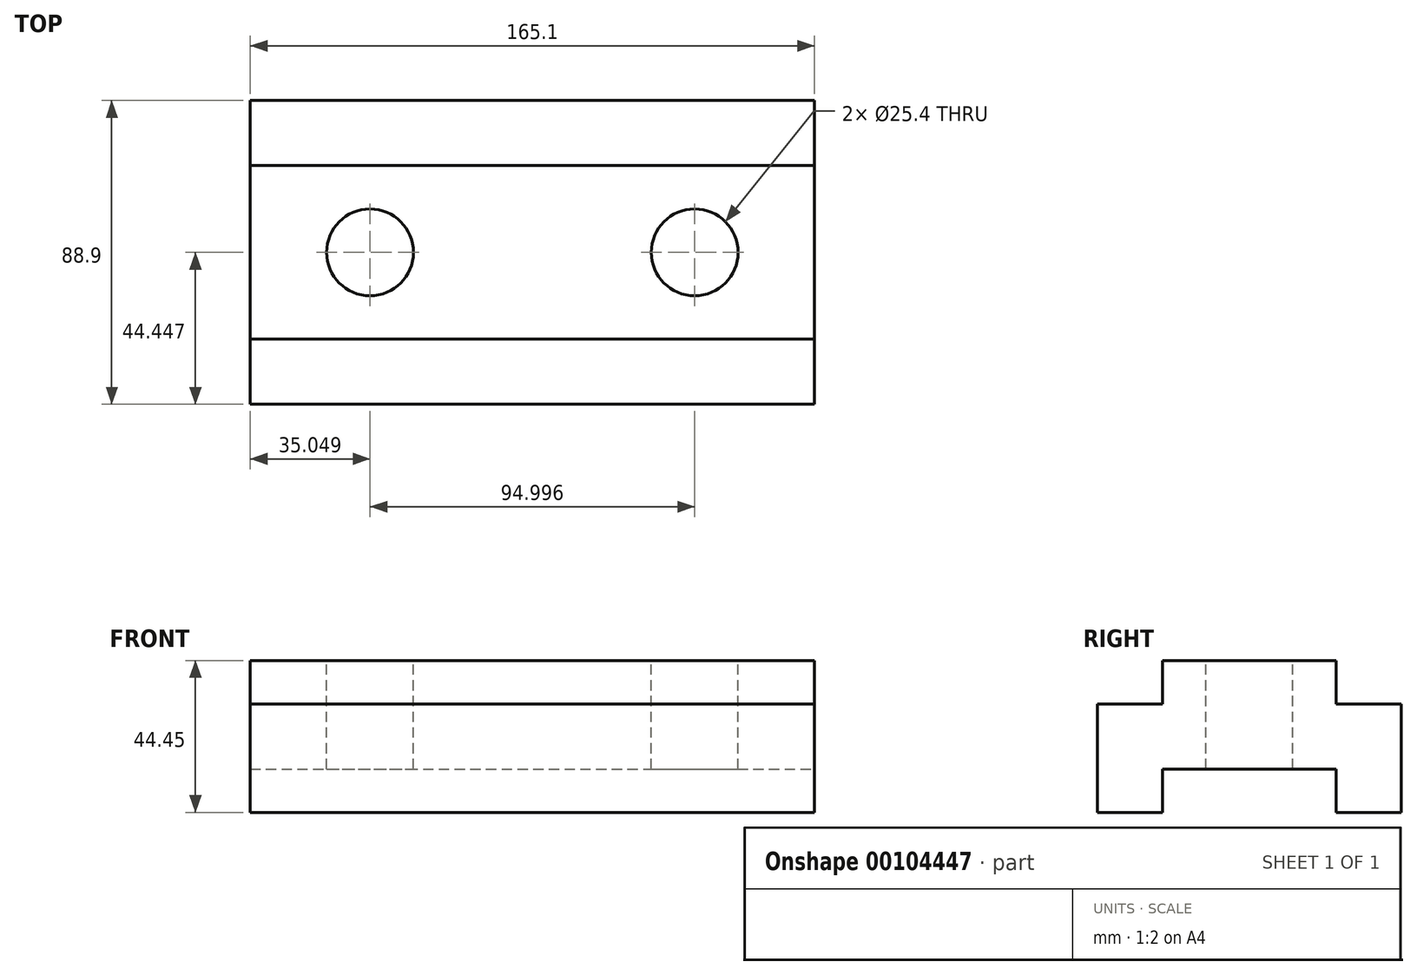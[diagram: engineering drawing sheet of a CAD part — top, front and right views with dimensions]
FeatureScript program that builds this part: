
annotation { "Feature Type Name" : "Feature", "Feature Type Description" : "" }
export const myFeature = defineFeature(function(context is Context, id is Id, definition is map)
    precondition{}
    {
        {
            var Q0;
            Q0=qCreatedBy(makeId("Top.planeOp"),FACE);
            var sketch = newSketch(context, id + "F0", { "sketchPlane" : qUnion([Q0])});
            skLineSegment(sketch, "E0.bottom", {"start": v(-108.37, 36.42) * mm, "end": v(56.73, 36.42) * mm});
            skLineSegment(sketch, "E0.top", {"start": v(-108.37, -52.48) * mm, "end": v(56.73, -52.48) * mm});
            skLineSegment(sketch, "E0.left", {"start": v(-108.37, 36.42) * mm, "end": v(-108.37, -52.48) * mm});
            skLineSegment(sketch, "E0.right", {"start": v(56.73, 36.42) * mm, "end": v(56.73, -52.48) * mm});
            skSolve(sketch);
        }
        {
            var Q0;
            Q0 = qSketchRegion(id + "F0", true);
            extrude(context, id + "F1", {"entities" : qUnion([Q0]), "depth" : 44.45 * mm});
        }
        {
            var Q0;
            Q0=makeQuery(id+"F1.opExtrude","SWEPT_FACE",FACE,{"disambiguationData":[OSD([sQuery(id+"F0.wireOp",EDGE,"E0.right")])]});
            var sketch = newSketch(context, id + "F2", { "sketchPlane" : qUnion([Q0])});
            skLineSegment(sketch, "E1", {"start": v(-52.48, 0) * mm, "end": v(-33.43, 0) * mm});
            skLineSegment(sketch, "E2", {"start": v(-33.43, 0) * mm, "end": v(17.37, 0) * mm});
            skLineSegment(sketch, "E3", {"start": v(-33.43, 0) * mm, "end": v(-33.43, 12.7) * mm});
            skLineSegment(sketch, "E4", {"start": v(-33.43, 12.7) * mm, "end": v(17.37, 12.7) * mm});
            skLineSegment(sketch, "E5", {"start": v(17.37, 12.7) * mm, "end": v(17.37, 0) * mm});
            skSolve(sketch);
        }
        {
            var Q0;
            Q0 = qSketchRegion(id + "F2", true);
            extrude(context, id + "F3", {"entities" : qUnion([Q0]), "operationType" : NewBodyOperationType.REMOVE, "oppositeDirection" : true, "depth" : 165.1 * mm});
        }
        {
            var Q0;
            Q0=makeQuery(id+"F1.opExtrude","SWEPT_FACE",FACE,{"disambiguationData":[OSD([sQuery(id+"F0.wireOp",EDGE,"E0.right")])]});
            var sketch = newSketch(context, id + "F4", { "sketchPlane" : qUnion([Q0])});
            skLineSegment(sketch, "E6", {"start": v(-52.48, 44.45) * mm, "end": v(-52.48, 31.75) * mm});
            skLineSegment(sketch, "E7", {"start": v(-52.48, 31.75) * mm, "end": v(-33.43, 31.75) * mm});
            skLineSegment(sketch, "E8", {"start": v(-33.43, 31.75) * mm, "end": v(-33.43, 44.45) * mm});
            skLineSegment(sketch, "E9", {"start": v(-33.43, 44.45) * mm, "end": v(-52.48, 44.45) * mm});
            skSolve(sketch);
        }
        {
            var Q0;
            Q0 = qSketchRegion(id + "F4", true);
            extrude(context, id + "F5", {"entities" : qUnion([Q0]), "operationType" : NewBodyOperationType.REMOVE, "oppositeDirection" : true, "depth" : 165.1 * mm});
        }
        {
            var Q0;
            Q0=makeQuery(id+"F1.opExtrude","SWEPT_FACE",FACE,{"disambiguationData":[OSD([sQuery(id+"F0.wireOp",EDGE,"E0.right")])]});
            var sketch = newSketch(context, id + "F6", { "sketchPlane" : qUnion([Q0])});
            skLineSegment(sketch, "E10", {"start": v(36.42, 44.45) * mm, "end": v(17.37, 44.45) * mm});
            skLineSegment(sketch, "E11", {"start": v(17.37, 44.45) * mm, "end": v(17.37, 31.75) * mm});
            skLineSegment(sketch, "E12", {"start": v(17.37, 31.75) * mm, "end": v(36.42, 31.75) * mm});
            skLineSegment(sketch, "E13", {"start": v(36.42, 31.75) * mm, "end": v(36.42, 44.45) * mm});
            skSolve(sketch);
        }
        {
            var Q0;
            Q0 = qSketchRegion(id + "F6", true);
            extrude(context, id + "F7", {"entities" : qUnion([Q0]), "operationType" : NewBodyOperationType.REMOVE, "oppositeDirection" : true, "depth" : 165.1 * mm});
        }
        {
            var Q0;
            Q0=makeQuery(id+"F1.opExtrude","CAP_FACE",FACE,{"disambiguationData":[OSD([sQuery(id+"F0.wireOp",EDGE,"E0.bottom"),sQuery(id+"F0.wireOp",EDGE,"E0.top"),sQuery(id+"F0.wireOp",EDGE,"E0.left"),sQuery(id+"F0.wireOp",EDGE,"E0.right")])],"isStart":false});
            var sketch = newSketch(context, id + "F8", { "sketchPlane" : qUnion([Q0])});
            skCircle(sketch, "E14", {"center": v(-73.32, -8.03) * mm, "radius": 12.7 * mm});
            skSolve(sketch);
        }
        {
            var Q0;
            Q0 = qSketchRegion(id + "F8", true);
            extrude(context, id + "F9", {"entities" : qUnion([Q0]), "operationType" : NewBodyOperationType.REMOVE, "oppositeDirection" : true, "depth" : 44.45 * mm});
        }
        {
            var Q0;
            Q0=makeQuery(id+"F1.opExtrude","CAP_FACE",FACE,{"disambiguationData":[OSD([sQuery(id+"F0.wireOp",EDGE,"E0.bottom"),sQuery(id+"F0.wireOp",EDGE,"E0.top"),sQuery(id+"F0.wireOp",EDGE,"E0.left"),sQuery(id+"F0.wireOp",EDGE,"E0.right")])],"isStart":false});
            var sketch = newSketch(context, id + "F10", { "sketchPlane" : qUnion([Q0])});
            skCircle(sketch, "E15", {"center": v(21.68, -8.03) * mm, "radius": 12.7 * mm});
            skSolve(sketch);
        }
        {
            var Q0;
            Q0=makeQuery(id+"F10.imprint","IMPRINT",FACE,{"disambiguationData":[TD([[makeQuery(id+"F10.imprint","IMPRINT",EDGE,{"derivedFrom":sQuery(id+"F10.wireOp",EDGE,"E15")}),1.0]])]});
            extrude(context, id + "F11", {"entities" : qUnion([Q0]), "operationType" : NewBodyOperationType.REMOVE, "oppositeDirection" : true, "depth" : 44.45 * mm});
        }
    });
